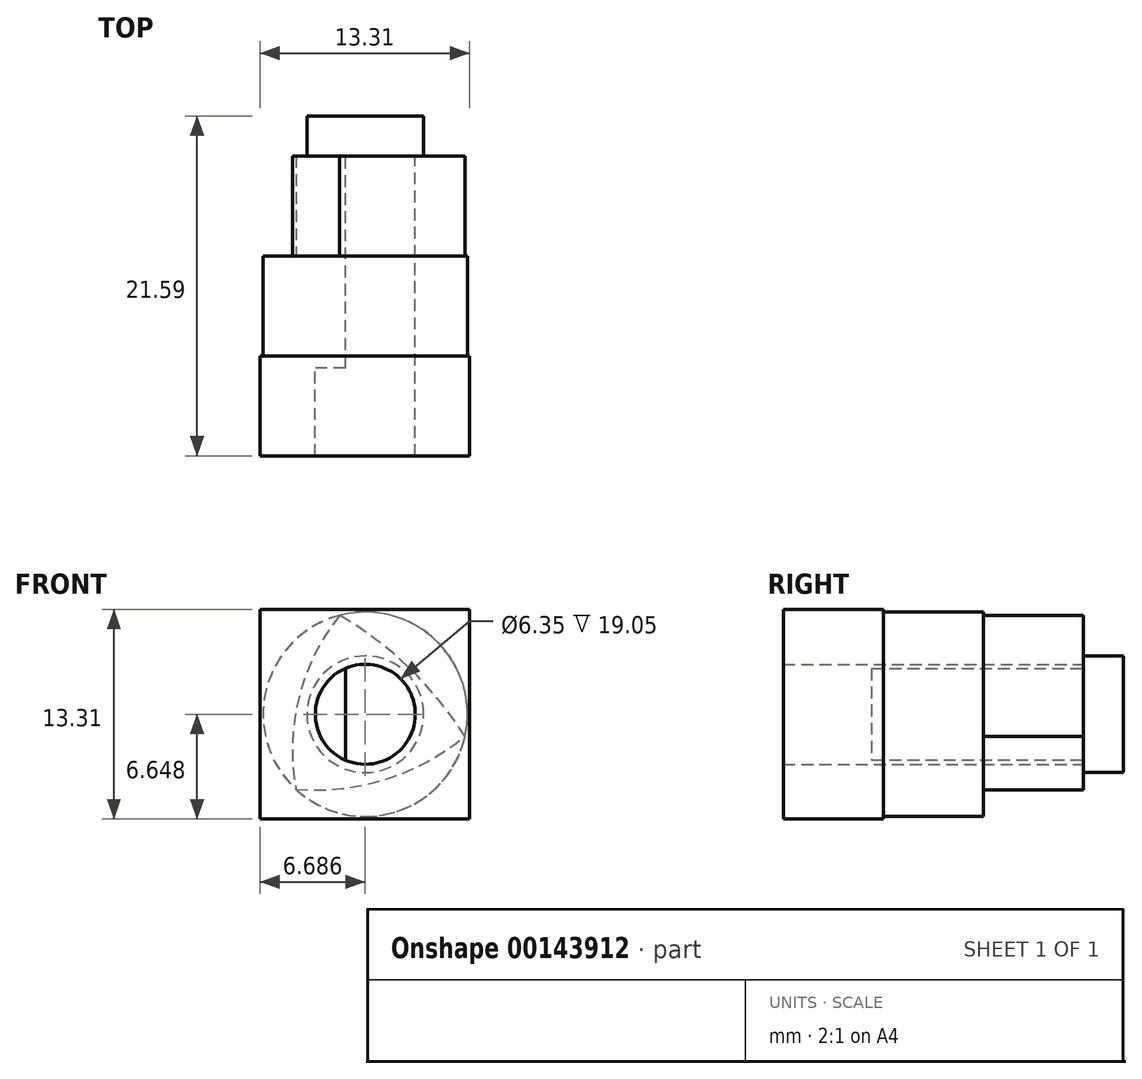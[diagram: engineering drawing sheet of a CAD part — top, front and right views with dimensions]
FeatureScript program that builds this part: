
annotation { "Feature Type Name" : "Feature", "Feature Type Description" : "" }
export const myFeature = defineFeature(function(context is Context, id is Id, definition is map)
    precondition{}
    {
        {
            var Q0;
            Q0=qCreatedBy(makeId("Front.planeOp"),FACE);
            var sketch = newSketch(context, id + "F0", { "sketchPlane" : qUnion([Q0])});
            skCircle(sketch, "E0", {"center": v(-30.53, 11.15) * mm, "radius": 3.18 * mm});
            skLineSegment(sketch, "E1", {"start": v(-31.8, 26.4) * mm, "end": v(-31.8, -9.04) * mm});
            skCircle(sketch, "E2", {"center": v(-30.53, 11.15) * mm, "radius": 6.49 * mm});
            skSolve(sketch);
        }
        {
            var Q0;
            {var subQ0=sQuery(id+"F0.wireOp",EDGE,"E1");var subQ1=sQuery(id+"F0.wireOp",EDGE,"E0");var subQ2=makeQuery(id+"F0.imprint","INTERSECT",VERTEX,{"disambiguationData":[OD(0.0)],"derivedFrom":[subQ1,subQ0]});Q0=makeQuery(id+"F0.imprint","IMPRINT",FACE,{"disambiguationData":[TD([[makeQuery(id+"F0.imprint","IMPRINT",EDGE,{"disambiguationData":[TD([[subQ2,-1.0]])],"derivedFrom":subQ1}),-1.0]])]});}
            var Q1;
            {var subQ0=sQuery(id+"F0.wireOp",EDGE,"E1");var subQ1=sQuery(id+"F0.wireOp",EDGE,"E0");var subQ2=makeQuery(id+"F0.imprint","INTERSECT",VERTEX,{"disambiguationData":[OD(0.0)],"derivedFrom":[subQ1,subQ0]});Q1=makeQuery(id+"F0.imprint","IMPRINT",FACE,{"disambiguationData":[TD([[makeQuery(id+"F0.imprint","IMPRINT",EDGE,{"disambiguationData":[TD([[subQ2,-1.0]])],"derivedFrom":subQ1}),1.0]])]});}
            var Q2;
            {var subQ0=sQuery(id+"F0.wireOp",EDGE,"E1");var subQ1=sQuery(id+"F0.wireOp",EDGE,"E0");var subQ2=makeQuery(id+"F0.imprint","INTERSECT",VERTEX,{"disambiguationData":[OD(0.0)],"derivedFrom":[subQ1,subQ0]});Q2=makeQuery(id+"F0.imprint","IMPRINT",FACE,{"disambiguationData":[TD([[makeQuery(id+"F0.imprint","IMPRINT",EDGE,{"disambiguationData":[TD([[subQ2,1.0]])],"derivedFrom":subQ1}),-1.0]])]});}
            extrude(context, id + "F1", {"entities" : qUnion([Q0, Q1, Q2]), "depth" : 6.35 * mm});
        }
        {
            var Q0;
            Q0=makeQuery(id+"F1.opExtrude","CAP_FACE",FACE,{"disambiguationData":[OSD([sQuery(id+"F0.wireOp",EDGE,"E0"),sQuery(id+"F0.wireOp",EDGE,"E1"),sQuery(id+"F0.wireOp",EDGE,"E2")])],"isStart":false});
            var sketch = newSketch(context, id + "F2", { "sketchPlane" : qUnion([Q0])});
            skLineSegment(sketch, "E3.bottom", {"start": v(-37.22, 17.8) * mm, "end": v(-23.91, 17.8) * mm});
            skLineSegment(sketch, "E3.top", {"start": v(-37.22, 4.5) * mm, "end": v(-23.91, 4.5) * mm});
            skLineSegment(sketch, "E3.left", {"start": v(-37.22, 17.8) * mm, "end": v(-37.22, 4.5) * mm});
            skLineSegment(sketch, "E3.right", {"start": v(-23.91, 17.8) * mm, "end": v(-23.91, 4.5) * mm});
            skSolve(sketch);
        }
        {
            var Q0;
            Q0=makeQuery(id+"F2.imprint","IMPRINT",FACE,{"disambiguationData":[TD([[makeQuery(id+"F2.imprint","IMPRINT",EDGE,{"derivedFrom":sQuery(id+"F2.wireOp",EDGE,"E3.bottom")}),-1.0]])]});
            var Q1;
            Q1=makeQuery(id+"F2.imprint","IMPRINT",FACE,{"disambiguationData":[TD([[makeQuery(id+"F2.imprint","IMPRINT",EDGE,{"derivedFrom":makeQuery(id+"F1.opExtrude","CAP_EDGE",EDGE,{"disambiguationData":[OSD([sQuery(id+"F0.wireOp",EDGE,"E0")])],"isStart":false})}),-1.0]])]});
            extrude(context, id + "F3", {"entities" : qUnion([Q0, Q1]), "operationType" : NewBodyOperationType.ADD, "depth" : 6.35 * mm});
        }
        {
            var Q0;
            {var subQ0=sQuery(id+"F0.wireOp",EDGE,"E1");var subQ1=sQuery(id+"F0.wireOp",EDGE,"E0");var subQ2=makeQuery(id+"F0.imprint","INTERSECT",VERTEX,{"disambiguationData":[OD(0.0)],"derivedFrom":[subQ1,subQ0]});Q0=makeQuery(id+"F0.imprint","IMPRINT",FACE,{"disambiguationData":[TD([[makeQuery(id+"F0.imprint","IMPRINT",EDGE,{"disambiguationData":[TD([[subQ2,-1.0]])],"derivedFrom":subQ1}),1.0]])]});}
            extrude(context, id + "F4", {"entities" : qUnion([Q0]), "operationType" : NewBodyOperationType.REMOVE, "depth" : 25.4 * mm});
        }
        {
            var Q0;
            {var subQ0=sQuery(id+"F0.wireOp",EDGE,"E1");var subQ1=sQuery(id+"F0.wireOp",EDGE,"E0");var subQ2=makeQuery(id+"F0.imprint","INTERSECT",VERTEX,{"disambiguationData":[OD(0.0)],"derivedFrom":[subQ1,subQ0]});Q0=makeQuery(id+"F0.imprint","IMPRINT",FACE,{"disambiguationData":[TD([[makeQuery(id+"F0.imprint","IMPRINT",EDGE,{"disambiguationData":[TD([[subQ2,-1.0]])],"derivedFrom":subQ1}),1.0]])]});}
            extrude(context, id + "F5", {"entities" : qUnion([Q0]), "operationType" : NewBodyOperationType.ADD, "depth" : 7.11 * mm});
        }
        {
            var Q0;
            {var subQ0=sQuery(id+"F0.wireOp",EDGE,"E1");var subQ1=sQuery(id+"F0.wireOp",EDGE,"E0");Q0=makeQuery(id+"F5.boolean.opBoolean","MERGE",FACE,{"derivedFrom":[makeQuery(id+"F1.opExtrude","CAP_FACE",FACE,{"disambiguationData":[OSD([subQ1,subQ0,sQuery(id+"F0.wireOp",EDGE,"E2")])],"isStart":true}),makeQuery(id+"F5.opExtrude","CAP_FACE",FACE,{"disambiguationData":[OSD([subQ1,subQ0])],"isStart":true})]});}
            var sketch = newSketch(context, id + "F6", { "sketchPlane" : qUnion([Q0])});
            skArc(sketch, "E4", {"start": v(24.2, 9.74) * mm, "mid": v(29.24, 7.02) * mm, "end": v(34.93, 6.38) * mm});
            skArc(sketch, "E5", {"start": v(34.93, 6.38) * mm, "mid": v(34.75, 12.2) * mm, "end": v(32.16, 17.43) * mm});
            skArc(sketch, "E6", {"start": v(32.16, 17.43) * mm, "mid": v(27.72, 14.06) * mm, "end": v(24.2, 9.74) * mm});
            skSolve(sketch);
        }
        {
            var Q0;
            Q0=makeQuery(id+"F6.imprint","IMPRINT",FACE,{"disambiguationData":[TD([[makeQuery(id+"F6.imprint","IMPRINT",EDGE,{"derivedFrom":sQuery(id+"F6.wireOp",EDGE,"E4")}),1.0]])]});
            extrude(context, id + "F7", {"entities" : qUnion([Q0]), "operationType" : NewBodyOperationType.ADD, "depth" : 6.35 * mm});
        }
        {
            var Q0;
            Q0=makeQuery(id+"F7.opExtrude","CAP_FACE",FACE,{"disambiguationData":[OSD([sQuery(id+"F0.wireOp",EDGE,"E0"),sQuery(id+"F0.wireOp",EDGE,"E1"),sQuery(id+"F6.wireOp",EDGE,"E4"),sQuery(id+"F6.wireOp",EDGE,"E5"),sQuery(id+"F6.wireOp",EDGE,"E6")])],"isStart":false});
            var sketch = newSketch(context, id + "F8", { "sketchPlane" : qUnion([Q0])});
            skCircle(sketch, "E7", {"center": v(30.53, 11.15) * mm, "radius": 3.7 * mm});
            skSolve(sketch);
        }
        {
            var Q0;
            Q0=makeQuery(id+"F8.imprint","IMPRINT",FACE,{"disambiguationData":[TD([[makeQuery(id+"F8.imprint","IMPRINT",EDGE,{"derivedFrom":sQuery(id+"F8.wireOp",EDGE,"E7")}),1.0]])]});
            var Q1;
            Q1=makeQuery(id+"F8.imprint","IMPRINT",FACE,{"disambiguationData":[TD([[makeQuery(id+"F8.imprint","IMPRINT",EDGE,{"derivedFrom":makeQuery(id+"F7.opExtrude","CAP_EDGE",EDGE,{"disambiguationData":[OSD([sQuery(id+"F0.wireOp",EDGE,"E1")])],"isStart":false})}),-1.0]])]});
            extrude(context, id + "F9", {"entities" : qUnion([Q0, Q1]), "operationType" : NewBodyOperationType.ADD, "depth" : 2.54 * mm});
        }
    });
